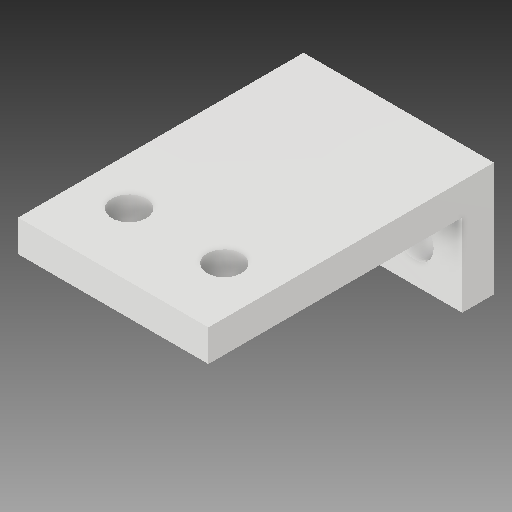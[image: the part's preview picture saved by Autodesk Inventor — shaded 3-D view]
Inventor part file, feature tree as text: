
AUTODESK INVENTOR PART (.ipt)
format: ipt  version: 2017 (Build 210142000, 142)  size: 130,560 bytes
history: native  units: in
note: dims shown in document units (in); Inventor stores cm internally (conversion verified against a paired STEP export)
features: sketch x3, hole x2, projected_geometry x2, extrude x1
ambient origin geometry x8: Origin, YZ Plane, XZ Plane, XY Plane, X Axis, Y Axis, Z Axis, Center Point
bodies: Solid1 (feature_tree)
feature tree (8):
  extrude  "Extrusion1"  Depth=1.125in
  hole  "Hole1"  [1 undecoded]
  hole  "Hole2"  [1 undecoded]
  sketch  "Sketch1"  dims[d0=0.45in d1=1.125in]
  sketch  "Sketch2"  dims[d2=0.325in d3=1.0in]
  projected_geometry  "Projected Loop1"
  sketch  "Sketch3"  dims[d4=0.75in d5=0.0in d6=0.375in d7=0.1875in d8=1.125in d11=0.135in d12=0.75in d13=0.375in d14=0.25in d15=0.5635in d16=1.0in d17=0.8108in d20=0.375in d21=0.1875in d22=0.1625in d23=0.1625in d24=0.15in d25=0.75in d26=0.375in d27=0.25in d28=0.5635in d29=1.0in d30=0.8108in d31=0.75in d32=0.75in d33=0.25in d34=0.25in d35=0.325in]
  projected_geometry  "Projected Loop2"
note: 2 required parameter values undecoded (feature->parameter linkage not recoverable at this tier; creation-order binding heuristic only, values carry confidence <= 0.55)
